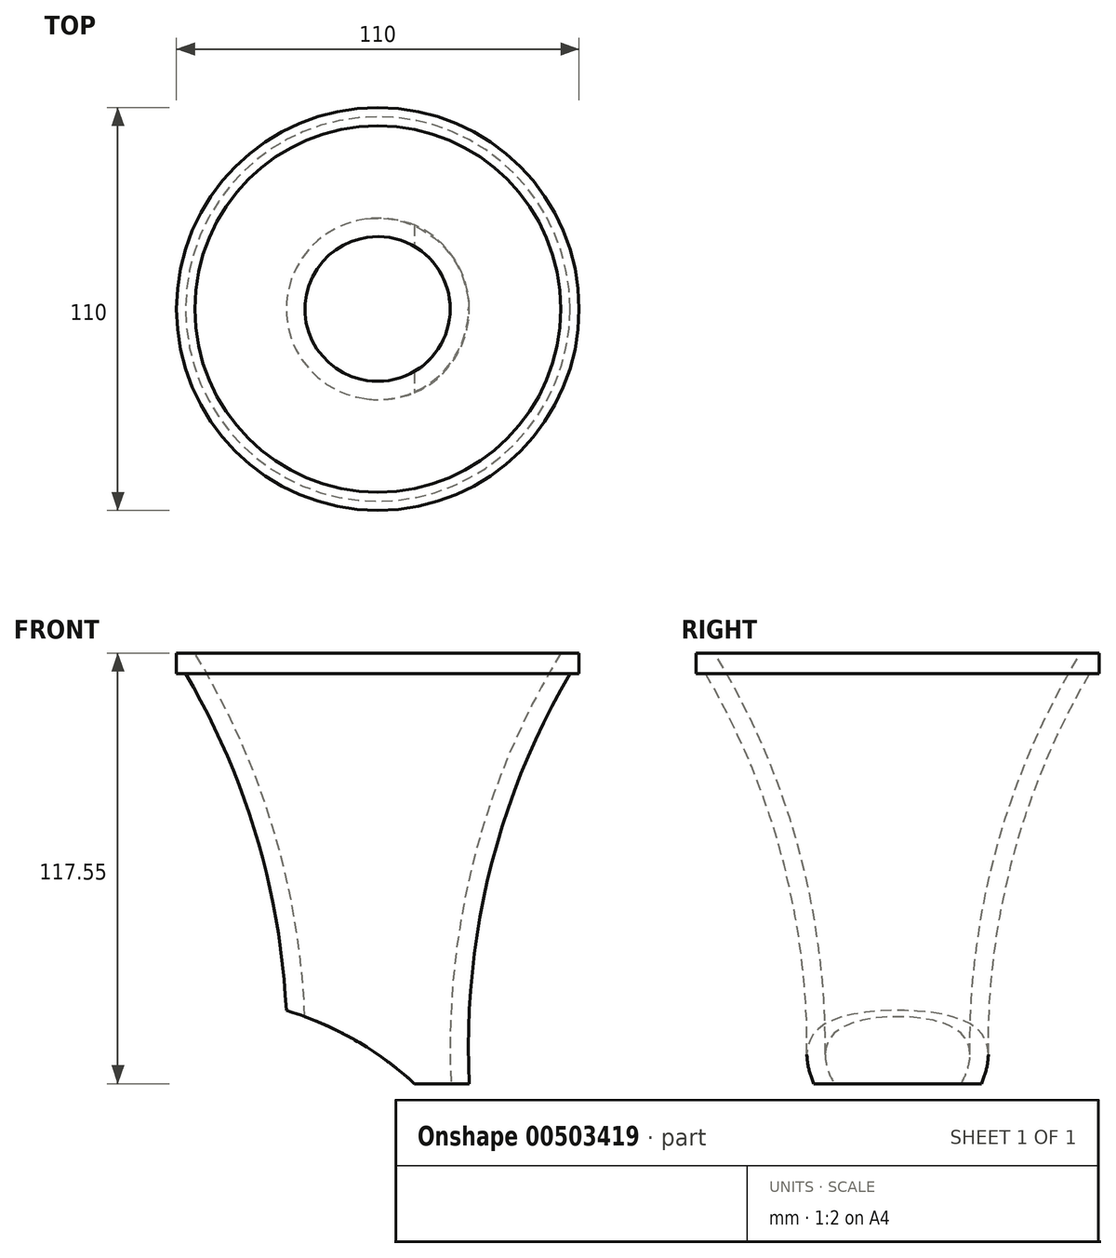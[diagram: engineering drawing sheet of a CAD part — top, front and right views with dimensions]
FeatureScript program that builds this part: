
annotation { "Feature Type Name" : "Feature", "Feature Type Description" : "" }
export const myFeature = defineFeature(function(context is Context, id is Id, definition is map)
    precondition{}
    {
        {
            var Q0;
            Q0=qCreatedBy(makeId("Front.planeOp"),FACE);
            var sketch = newSketch(context, id + "F0", { "sketchPlane" : qUnion([Q0])});
            skLineSegment(sketch, "E0", {"start": v(-50, 5.55) * mm, "end": v(-55, 5.55) * mm});
            skLineSegment(sketch, "E1", {"start": v(-55, 5.55) * mm, "end": v(-55, 0) * mm});
            skLineSegment(sketch, "E2", {"start": v(-55, 0) * mm, "end": v(-52.5, 0) * mm});
            skArc(sketch, "E3", {"start": v(-25, -112) * mm, "mid": v(-30.57, -54) * mm, "end": v(-52.5, 0) * mm});
            skLineSegment(sketch, "E4", {"start": v(0, 48.58) * mm, "end": v(0, -126.75) * mm, "construction": true});
            skArc(sketch, "E5", {"start": v(-20, -112) * mm, "mid": v(-26.18, -50.97) * mm, "end": v(-50, 5.55) * mm});
            skLineSegment(sketch, "E6", {"start": v(-25, -112) * mm, "end": v(-20, -112) * mm});
            skSolve(sketch);
        }
        {
            var Q0;
            Q0 = qSketchRegion(id + "F0", true);
            var Q1;
            Q1=sQuery(id+"F0.wireOp",EDGE,"E4");
            revolve(context, id + "F1", {"entities" : qUnion([Q0]), "axis" : qUnion([Q1]), "revolveType" : RevolveType.FULL});
        }
        {
            var Q0;
            Q0=qCreatedBy(makeId("Front.planeOp"),FACE);
            var sketch = newSketch(context, id + "F2", { "sketchPlane" : qUnion([Q0])});
            skArc(sketch, "E7", {"start": v(10, -112) * mm, "mid": v(-6.37, -100.01) * mm, "end": v(-25, -92) * mm});
            skLineSegment(sketch, "E8", {"start": v(-25, -92) * mm, "end": v(-25, -112) * mm});
            skLineSegment(sketch, "E9", {"start": v(-25, -112) * mm, "end": v(10, -112) * mm});
            skSolve(sketch);
        }
        {
            var Q0;
            Q0 = qSketchRegion(id + "F2", true);
            extrude(context, id + "F3", {"entities" : qUnion([Q0]), "operationType" : NewBodyOperationType.REMOVE, "endBound" : BoundingType.SYMMETRIC, "oppositeDirection" : true, "depth" : 50 * mm});
        }
    });
